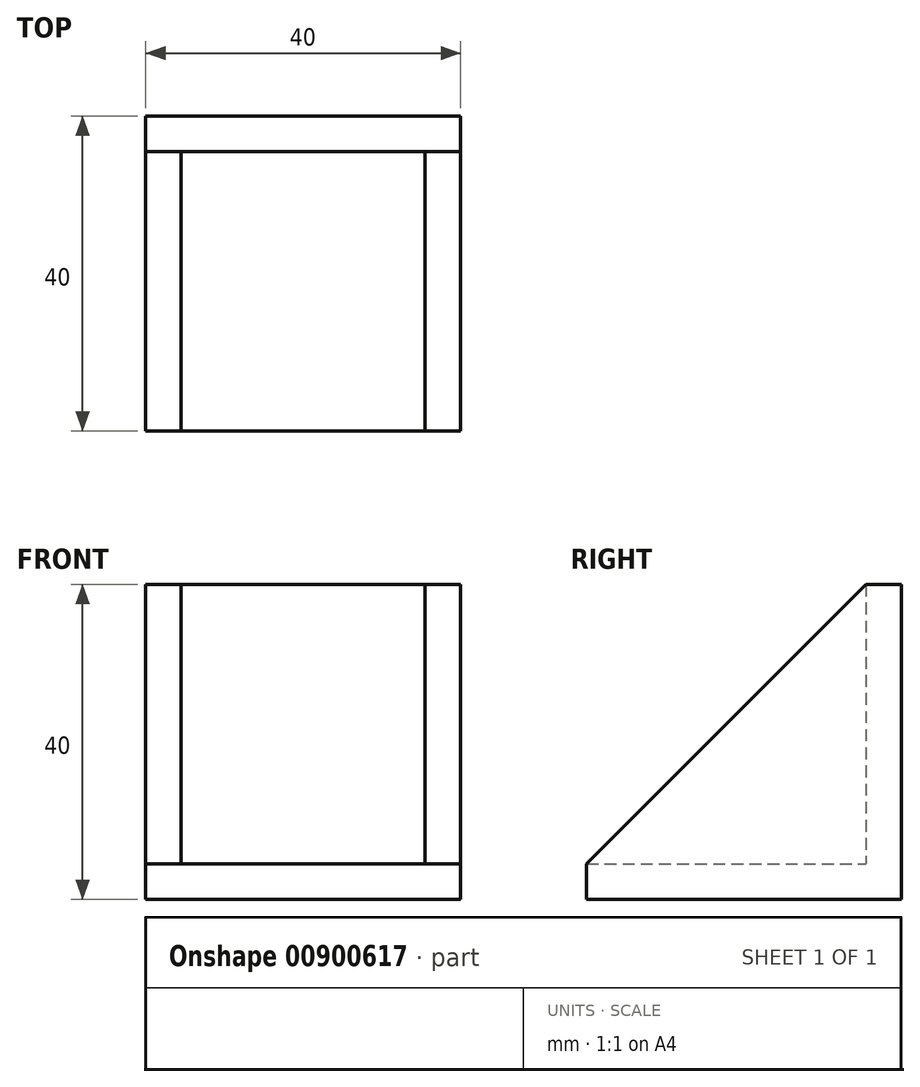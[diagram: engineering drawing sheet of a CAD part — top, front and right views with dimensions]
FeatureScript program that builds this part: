
annotation { "Feature Type Name" : "Feature", "Feature Type Description" : "" }
export const myFeature = defineFeature(function(context is Context, id is Id, definition is map)
    precondition{}
    {
        {
            var Q0;
            Q0=qCreatedBy(makeId("Top.planeOp"),FACE);
            var sketch = newSketch(context, id + "F0", { "sketchPlane" : qUnion([Q0])});
            skLineSegment(sketch, "E0.bottom", {"start": v(20, -20) * mm, "end": v(-20, -20) * mm});
            skLineSegment(sketch, "E0.top", {"start": v(20, 20) * mm, "end": v(-20, 20) * mm});
            skLineSegment(sketch, "E0.left", {"start": v(20, -20) * mm, "end": v(20, 20) * mm});
            skLineSegment(sketch, "E0.right", {"start": v(-20, -20) * mm, "end": v(-20, 20) * mm});
            skPoint(sketch, "E0.middle", {"position": v(0, 0) * mm});
            skSolve(sketch);
        }
        {
            var Q0;
            Q0=makeQuery(id+"F0.imprint","IMPRINT",FACE,{"disambiguationData":[TD([[makeQuery(id+"F0.imprint","IMPRINT",EDGE,{"derivedFrom":sQuery(id+"F0.wireOp",EDGE,"E0.bottom")}),-1.0]])]});
            extrude(context, id + "F1", {"entities" : qUnion([Q0]), "depth" : 40 * mm, "offsetDistance" : 25 * mm});
        }
        {
            var Q0;
            Q0=makeQuery(id+"F1.opExtrude","SWEPT_FACE",FACE,{"disambiguationData":[OSD([sQuery(id+"F0.wireOp",EDGE,"E0.bottom")])]});
            var Q1;
            Q1=makeQuery(id+"F1.opExtrude","CAP_FACE",FACE,{"disambiguationData":[OSD([sQuery(id+"F0.wireOp",EDGE,"E0.bottom"),sQuery(id+"F0.wireOp",EDGE,"E0.top"),sQuery(id+"F0.wireOp",EDGE,"E0.left"),sQuery(id+"F0.wireOp",EDGE,"E0.right")])],"isStart":false});
            shell(context, id + "F2", {"entities" : qUnion([Q0, Q1]), "thickness" : 4.5 * mm});
        }
        {
            var Q0;
            Q0=makeQuery(id+"F1.opExtrude","CAP_EDGE",EDGE,{"disambiguationData":[OSD([sQuery(id+"F0.wireOp",EDGE,"E0.bottom")])],"isStart":false});
            var Q1;
            {var subQ0=sQuery(id+"F0.wireOp",EDGE,"E0.bottom");Q1=makeQuery(id+"F2.opShell","OFFSET_EDGE",EDGE,{"disambiguationData":[OSD([subQ0]),TDD([makeQuery(id+"F1.opExtrude","CAP_EDGE",EDGE,{"disambiguationData":[OSD([subQ0])],"isStart":false})])]});}
            chamfer(context, id + "F3", {"entities" : qUnion([Q0, Q1]), "width" : 35.5 * mm, "tangentPropagation" : true});
        }
    });
